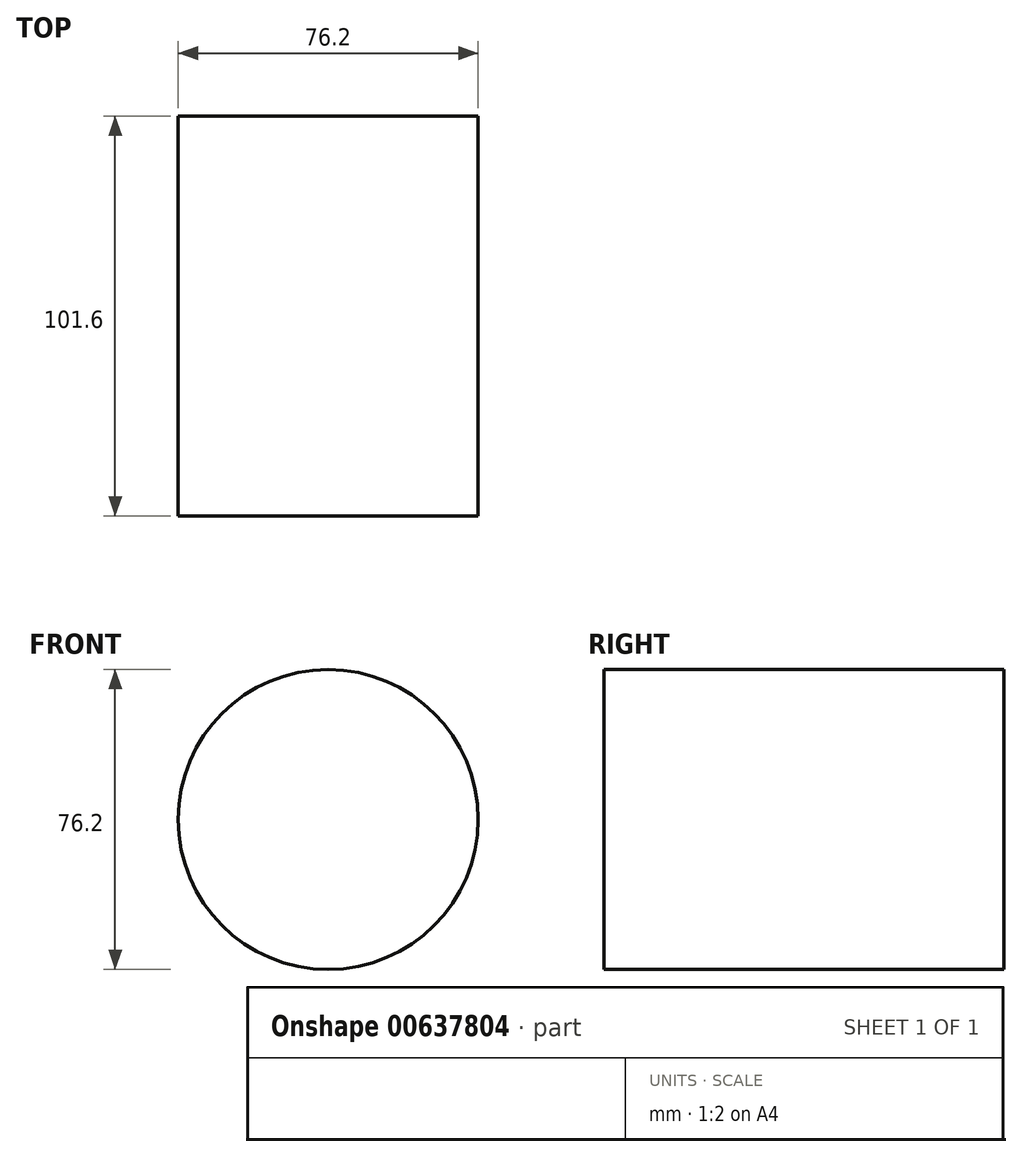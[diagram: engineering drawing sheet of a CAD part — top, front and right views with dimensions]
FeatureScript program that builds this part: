
annotation { "Feature Type Name" : "Feature", "Feature Type Description" : "" }
export const myFeature = defineFeature(function(context is Context, id is Id, definition is map)
    precondition{}
    {
        {
            var Q0;
            Q0=qCreatedBy(makeId("Front.planeOp"),FACE);
            var sketch = newSketch(context, id + "F0", { "sketchPlane" : qUnion([Q0])});
            skCircle(sketch, "E0", {"center": v(0, 0) * mm, "radius": 38.1 * mm});
            skSolve(sketch);
        }
        {
            var Q0;
            Q0 = qSketchRegion(id + "F0", true);
            extrude(context, id + "F1", {"entities" : qUnion([Q0]), "depth" : 101.6 * mm, "offsetDistance" : 25.4 * mm});
        }
    });
